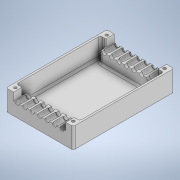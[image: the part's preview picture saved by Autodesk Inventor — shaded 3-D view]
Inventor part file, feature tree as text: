
AUTODESK INVENTOR PART (.ipt)
format: ipt  version: 2021 (Build 250183000, 183)  size: 427,520 bytes
history: native  units: mm
features: extrude x8, sketch x8, fillet x5
ambient origin geometry x8: Origin, YZ Plane, XZ Plane, XY Plane, X Axis, Y Axis, Z Axis, Center Point
bodies: Body1 (feature_tree)
feature tree (21):
  extrude  "Extrusion20"  Depth=2.0mm
  extrude  "Extrusion21"  Depth=2.0mm TaperAngle=0.0deg
  extrude  "Extrusion24"  Depth=2.0mm TaperAngle=0.0deg
  fillet  "Fillet12"  Radius=3.0mm
  extrude  "Extrusion25"  Depth=3.0mm
  fillet  "Fillet13"  Radius=3.0mm
  extrude  "Extrusion26"  Depth=2.0mm
  extrude  "Extrusion27"  Depth=56.0mm
  extrude  "Extrusion28"  Depth=15.0mm
  extrude  "Extrusion29"  Depth=2.0mm
  fillet  "Fillet14"  Radius=8.0mm
  fillet  "Fillet15"  Radius=2.0mm
  fillet  "Fillet16"  Radius=56.0mm
  sketch  "Sketch26"  dims[d181=2.0mm d182=2.0mm d184=2.0mm d186=2.0mm d187=8.0mm d190=8.0mm d193=8.0mm d196=8.0mm d249=108.0mm]
  sketch  "Sketch27"  dims[d250=72.0mm d251=2.0mm d252=0.0mm]
  sketch  "Sketch30"  dims[d253=2.0mm d254=20.0mm d255=0.0mm d292=3.0mm]
  sketch  "Sketch31"  dims[d293=3.0mm d294=3.0mm d295=3.0mm]
  sketch  "Sketch32"  dims[d296=20.0mm d297=0.0mm d298=2.0mm]
  sketch  "Sketch33"  dims[d299=56.0mm d300=56.0mm]
  sketch  "Sketch34"  dims[d301=8.0mm d302=15.0mm]
  sketch  "Sketch35"  dims[d303=8.0mm d304=15.0mm d305=8.0mm d306=0.0mm d307=2.0mm d308=56.0mm d309=15.0mm d310=15.0mm d311=12.0mm d312=0.0mm d313=6.0mm d314=4.0mm d315=70.0mm d317=8.0mm d318=10.0mm d320=10.0mm d322=1000.0mm d323=0.0mm d324=1.0mm d325=1.0mm d326=3.0mm d327=3.0mm d328=8.0mm d329=0.0mm d330=4.0mm d331=4.5mm d332=70.0mm d334=8.0mm d335=10.0mm d337=10.0mm d339=1000.0mm d340=0.0mm d341=2.0mm d342=2.0mm d343=2.0mm]
